# Revit family: Sanitary_Wash-basins_DURAVIT-AG_Bacino-Above-Counter-Bathroom-Sink-032542ed
name_source: partatom
category: Plumbing Fixtures
revit_build: Autodesk Revit 2018 (Build: 20190510_1515(x64)
units: mm (PartAtom-declared; Revit-internal decimal feet)

## family parameters
Always vertical = No
Cut with Voids When Loaded = No
OmniClass Number = 23.31.13.00
OmniClass Title = Sinks
Part Type = Normal
Room Calculation Point = No
Round Connector Dimension = Use Diameter
Shared = No
Work Plane-Based = Yes

## types (2) — shared parameters
BIMobject category = Wash basins
Connector Description = Water outlet
Date of publishing = 08.09.2020 00:00:00
Default Elevation = 1219.2 mm  [stored 4 ft]
Details material = Duravit - Metal - 10 - Chrome
ETIM classification = EC011550 | Washbasin
Edition number = 1
IFC Classification = Sanitary Terminal
Installation instructions = https://pro.duravit.com
Manufacturer = Duravit
Manufacturer name = DURAVIT AG
Masterformat 2014 Code = 22 41 16.13
Masterformat 2014 Description = Residential Lavatories
Material main = Ceramics
Model = Bacino Above-Counter Bathroom Sink - 032542
OmniClass Code = 23-31 13 00
OmniClass Description = Sinks
Outlet Diameter = 32 mm
Product Guid = da44b9e0-7b13-4d77-b532-43e246e1c491
Product SKU = bacino-above-counter-bathroom-sink-032542
Product certification = https://pro.duravit.com
Product data url = https://bimobject.com
Product family = Bacino
Product group = Washbowl
Product name = Bacino Above-Counter Bathroom Sink - 032542
Product url = https://pro.duravit.com
QR code = https://bimobject.com
Technical description = https://pro.duravit.com
UNSPSC Code = 30181504
URL = https://www.duravit.com
Uniclass 2015 Code = Pr_40_20_96
Uniclass 2015 Name = Wash basins, sinks and troughs
Uniformat II Code = E1010
Uniformat II Description = Commercial Equipment
Weight Net (Kg) = 7
Youtube clip = https://pro.duravit.com

## per-type parameters (varying)
| type | Description | Main material |
| 00 - White Alpin WonderGliss | Duravit Bacino Washbowl 420 mm White High Gloss, Number of faucet holes per wash area: 0, Overflow, WonderGliss - 03254200001 | Duravit - Ceramic - 00 - White Alpin WonderGliss |
| 00 - White Alpin | Duravit Bacino Washbowl 420 mm White High Gloss, Number of faucet holes per wash area: 0, Overflow - 0325420000 | Duravit - Ceramic - 00 - White Alpin |

note: [stored X ft] marks values corroborated as IEEE doubles in the binary element streams (Revit-internal decimal feet)

## geometry (parser evidence)
native form markers: Sweep x4
no freeform markers — native parametric forms only
